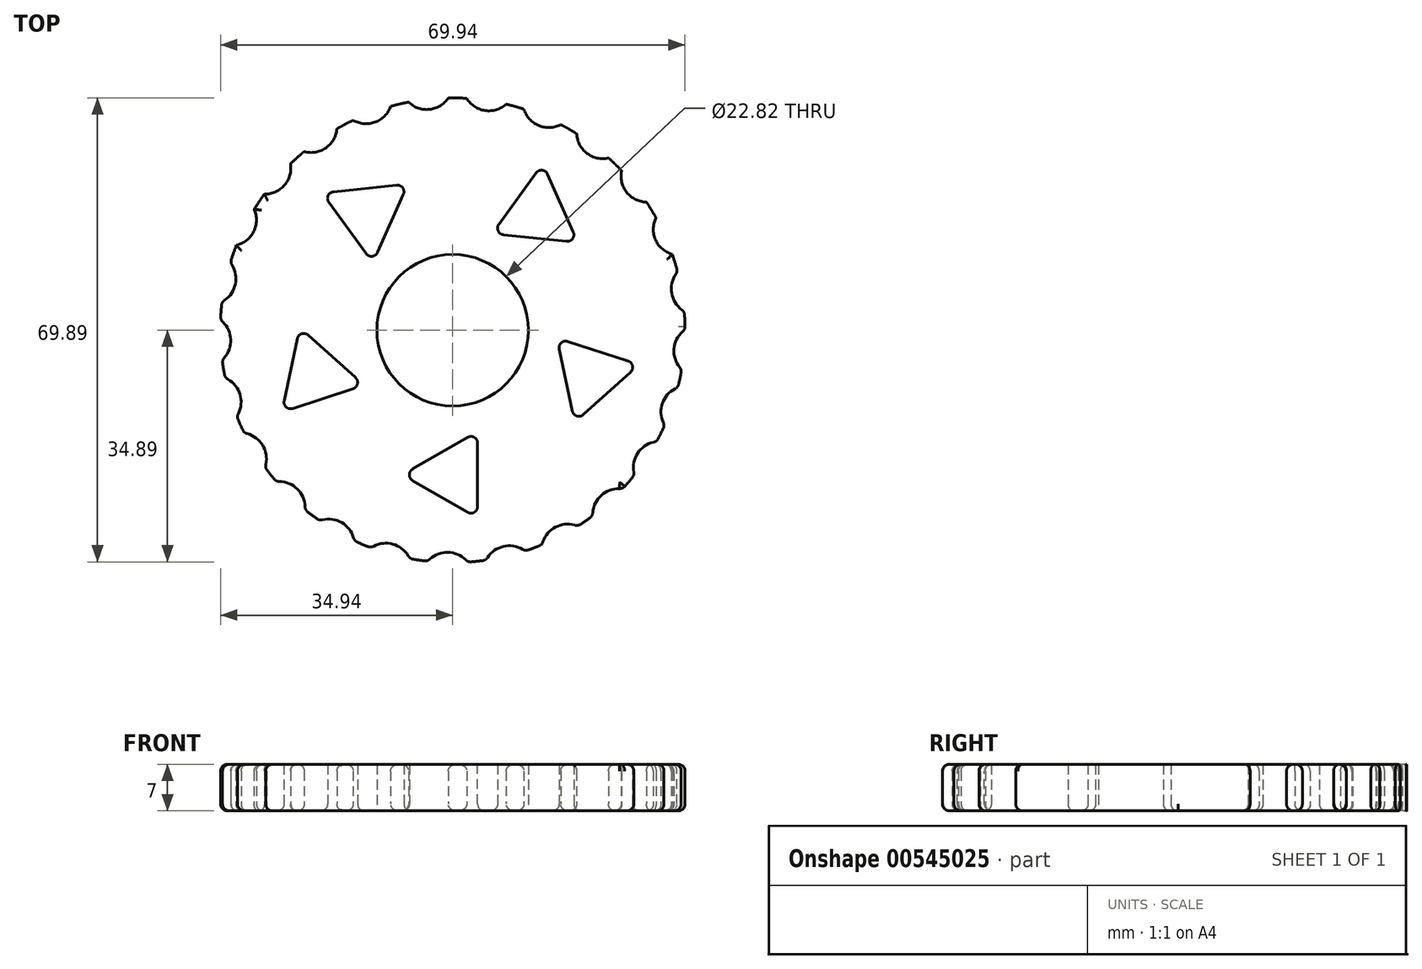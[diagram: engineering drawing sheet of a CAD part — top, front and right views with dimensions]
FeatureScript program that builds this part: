
annotation { "Feature Type Name" : "Feature", "Feature Type Description" : "" }
export const myFeature = defineFeature(function(context is Context, id is Id, definition is map)
    precondition{}
    {
        {
            var Q0;
            Q0=qCreatedBy(makeId("Top.planeOp"),FACE);
            var sketch = newSketch(context, id + "F0", { "sketchPlane" : qUnion([Q0])});
            skCircle(sketch, "E0", {"center": v(0, 0) * mm, "radius": 35 * mm});
            skCircle(sketch, "E1", {"center": v(0, 0) * mm, "radius": 11.41 * mm});
            skCircle(sketch, "E2", {"center": v(-36.54, 7.77) * mm, "radius": 3.9 * mm});
            skSolve(sketch);
        }
        {
            var Q0;
            Q0=makeQuery(id+"F0.imprint","IMPRINT",FACE,{"disambiguationData":[TD([[makeQuery(id+"F0.imprint","IMPRINT",EDGE,{"derivedFrom":sQuery(id+"F0.wireOp",EDGE,"E1")}),-1.0]])]});
            extrude(context, id + "F1", {"entities" : qUnion([Q0]), "depth" : 7 * mm, "offsetDistance" : 25 * mm});
        }
        {
            var Q0;
            Q0=makeQuery(id+"F1.opExtrude","SWEPT_FACE",FACE,{"disambiguationData":[OSD([sQuery(id+"F0.wireOp",EDGE,"E2")])]});
            var Q1;
            Q1=makeQuery(id+"F1.opExtrude","SWEPT_FACE",FACE,{"disambiguationData":[OSD([sQuery(id+"F0.wireOp",EDGE,"E0")])]});
            circularPattern(context, id + "F2", {"patternType" : PatternType.FACE, "faces" : qUnion([Q0]), "axis" : qUnion([Q1]), "angle" : 360 * degree, "instanceCount" : 25, "oppositeDirection" : true, "equalSpace" : true});
        }
        {
            var Q0;
            Q0=makeQuery(id+"F1.opExtrude","CAP_FACE",FACE,{"disambiguationData":[OSD([sQuery(id+"F0.wireOp",EDGE,"E0"),sQuery(id+"F0.wireOp",EDGE,"E1"),sQuery(id+"F0.wireOp",EDGE,"E2")])],"isStart":false});
            var sketch = newSketch(context, id + "F3", { "sketchPlane" : qUnion([Q0])});
            skCircle(sketch, "E3.cCircle", {"center": v(0, -21.78) * mm, "radius": 3.76 * mm, "construction": true});
            skLineSegment(sketch, "E3.0", {"start": v(3.76, -15.27) * mm, "end": v(3.76, -28.3) * mm});
            skLineSegment(sketch, "E3.1", {"start": v(3.76, -28.3) * mm, "end": v(-7.52, -21.78) * mm});
            skLineSegment(sketch, "E3.2", {"start": v(-7.52, -21.78) * mm, "end": v(3.76, -15.27) * mm});
            skPoint(sketch, "E3.0.midPoint", {"position": v(3.76, -21.78) * mm});
            skSolve(sketch);
        }
        {
            var Q0;
            Q0 = qSketchRegion(id + "F3", true);
            extrude(context, id + "F4", {"entities" : qUnion([Q0]), "operationType" : NewBodyOperationType.REMOVE, "oppositeDirection" : true, "depth" : 25 * mm, "offsetDistance" : 25 * mm});
        }
        {
            var Q0;
            Q0=makeQuery(id+"F4.boolean.opBoolean","COPY",FACE,{"derivedFrom":makeQuery(id+"F4.opExtrude","SWEPT_FACE",FACE,{"disambiguationData":[OSD([sQuery(id+"F3.wireOp",EDGE,"E3.2")])]})});
            var Q1;
            Q1=makeQuery(id+"F4.boolean.opBoolean","COPY",FACE,{"derivedFrom":makeQuery(id+"F4.opExtrude","SWEPT_FACE",FACE,{"disambiguationData":[OSD([sQuery(id+"F3.wireOp",EDGE,"E3.0")])]})});
            var Q2;
            Q2=makeQuery(id+"F4.boolean.opBoolean","COPY",FACE,{"derivedFrom":makeQuery(id+"F4.opExtrude","SWEPT_FACE",FACE,{"disambiguationData":[OSD([sQuery(id+"F3.wireOp",EDGE,"E3.1")])]})});
            var Q3;
            Q3=makeQuery(id+"F1.opExtrude","CAP_EDGE",EDGE,{"disambiguationData":[OSD([sQuery(id+"F0.wireOp",EDGE,"E1")])],"isStart":false});
            circularPattern(context, id + "F5", {"patternType" : PatternType.FACE, "faces" : qUnion([Q0, Q1, Q2]), "axis" : qUnion([Q3]), "angle" : 360 * degree, "instanceCount" : 5, "equalSpace" : true});
        }
        {
            var Q0;
            Q0=makeQuery(id+"F5.opPattern","COPY",EDGE,{"derivedFrom":makeQuery(id+"F4.boolean.opBoolean","COPY",EDGE,{"derivedFrom":makeQuery(id+"F4.opExtrude","SWEPT_EDGE",EDGE,{"disambiguationData":[OSD([sQuery(id+"F3.wireOp",EDGE,"E3.1"),sQuery(id+"F3.wireOp",EDGE,"E3.2")])]})}),"instanceName":"4"});
            var Q1;
            Q1=makeQuery(id+"F5.opPattern","COPY",EDGE,{"derivedFrom":makeQuery(id+"F4.boolean.opBoolean","COPY",EDGE,{"derivedFrom":makeQuery(id+"F4.opExtrude","SWEPT_EDGE",EDGE,{"disambiguationData":[OSD([sQuery(id+"F3.wireOp",EDGE,"E3.0"),sQuery(id+"F3.wireOp",EDGE,"E3.2")])]})}),"instanceName":"4"});
            var Q2;
            Q2=makeQuery(id+"F5.opPattern","COPY",EDGE,{"derivedFrom":makeQuery(id+"F4.boolean.opBoolean","COPY",EDGE,{"derivedFrom":makeQuery(id+"F4.opExtrude","SWEPT_EDGE",EDGE,{"disambiguationData":[OSD([sQuery(id+"F3.wireOp",EDGE,"E3.0"),sQuery(id+"F3.wireOp",EDGE,"E3.1")])]})}),"instanceName":"4"});
            var Q3;
            Q3=makeQuery(id+"F5.opPattern","COPY",EDGE,{"derivedFrom":makeQuery(id+"F4.boolean.opBoolean","COPY",EDGE,{"derivedFrom":makeQuery(id+"F4.opExtrude","SWEPT_EDGE",EDGE,{"disambiguationData":[OSD([sQuery(id+"F3.wireOp",EDGE,"E3.1"),sQuery(id+"F3.wireOp",EDGE,"E3.2")])]})}),"instanceName":"3"});
            var Q4;
            Q4=makeQuery(id+"F5.opPattern","COPY",EDGE,{"derivedFrom":makeQuery(id+"F4.boolean.opBoolean","COPY",EDGE,{"derivedFrom":makeQuery(id+"F4.opExtrude","SWEPT_EDGE",EDGE,{"disambiguationData":[OSD([sQuery(id+"F3.wireOp",EDGE,"E3.0"),sQuery(id+"F3.wireOp",EDGE,"E3.2")])]})}),"instanceName":"3"});
            var Q5;
            Q5=makeQuery(id+"F5.opPattern","COPY",EDGE,{"derivedFrom":makeQuery(id+"F4.boolean.opBoolean","COPY",EDGE,{"derivedFrom":makeQuery(id+"F4.opExtrude","SWEPT_EDGE",EDGE,{"disambiguationData":[OSD([sQuery(id+"F3.wireOp",EDGE,"E3.0"),sQuery(id+"F3.wireOp",EDGE,"E3.1")])]})}),"instanceName":"3"});
            var Q6;
            Q6=makeQuery(id+"F5.opPattern","COPY",EDGE,{"derivedFrom":makeQuery(id+"F4.boolean.opBoolean","COPY",EDGE,{"derivedFrom":makeQuery(id+"F4.opExtrude","SWEPT_EDGE",EDGE,{"disambiguationData":[OSD([sQuery(id+"F3.wireOp",EDGE,"E3.0"),sQuery(id+"F3.wireOp",EDGE,"E3.1")])]})}),"instanceName":"2"});
            var Q7;
            Q7=makeQuery(id+"F5.opPattern","COPY",EDGE,{"derivedFrom":makeQuery(id+"F4.boolean.opBoolean","COPY",EDGE,{"derivedFrom":makeQuery(id+"F4.opExtrude","SWEPT_EDGE",EDGE,{"disambiguationData":[OSD([sQuery(id+"F3.wireOp",EDGE,"E3.1"),sQuery(id+"F3.wireOp",EDGE,"E3.2")])]})}),"instanceName":"2"});
            var Q8;
            Q8=makeQuery(id+"F5.opPattern","COPY",EDGE,{"derivedFrom":makeQuery(id+"F4.boolean.opBoolean","COPY",EDGE,{"derivedFrom":makeQuery(id+"F4.opExtrude","SWEPT_EDGE",EDGE,{"disambiguationData":[OSD([sQuery(id+"F3.wireOp",EDGE,"E3.0"),sQuery(id+"F3.wireOp",EDGE,"E3.2")])]})}),"instanceName":"2"});
            var Q9;
            Q9=makeQuery(id+"F5.opPattern","COPY",EDGE,{"derivedFrom":makeQuery(id+"F4.boolean.opBoolean","COPY",EDGE,{"derivedFrom":makeQuery(id+"F4.opExtrude","SWEPT_EDGE",EDGE,{"disambiguationData":[OSD([sQuery(id+"F3.wireOp",EDGE,"E3.0"),sQuery(id+"F3.wireOp",EDGE,"E3.2")])]})}),"instanceName":"1"});
            var Q10;
            Q10=makeQuery(id+"F5.opPattern","COPY",EDGE,{"derivedFrom":makeQuery(id+"F4.boolean.opBoolean","COPY",EDGE,{"derivedFrom":makeQuery(id+"F4.opExtrude","SWEPT_EDGE",EDGE,{"disambiguationData":[OSD([sQuery(id+"F3.wireOp",EDGE,"E3.0"),sQuery(id+"F3.wireOp",EDGE,"E3.1")])]})}),"instanceName":"1"});
            var Q11;
            Q11=makeQuery(id+"F5.opPattern","COPY",EDGE,{"derivedFrom":makeQuery(id+"F4.boolean.opBoolean","COPY",EDGE,{"derivedFrom":makeQuery(id+"F4.opExtrude","SWEPT_EDGE",EDGE,{"disambiguationData":[OSD([sQuery(id+"F3.wireOp",EDGE,"E3.1"),sQuery(id+"F3.wireOp",EDGE,"E3.2")])]})}),"instanceName":"1"});
            var Q12;
            Q12=makeQuery(id+"F4.boolean.opBoolean","COPY",EDGE,{"derivedFrom":makeQuery(id+"F4.opExtrude","SWEPT_EDGE",EDGE,{"disambiguationData":[OSD([sQuery(id+"F3.wireOp",EDGE,"E3.0"),sQuery(id+"F3.wireOp",EDGE,"E3.2")])]})});
            var Q13;
            Q13=makeQuery(id+"F4.boolean.opBoolean","COPY",EDGE,{"derivedFrom":makeQuery(id+"F4.opExtrude","SWEPT_EDGE",EDGE,{"disambiguationData":[OSD([sQuery(id+"F3.wireOp",EDGE,"E3.1"),sQuery(id+"F3.wireOp",EDGE,"E3.2")])]})});
            var Q14;
            Q14=makeQuery(id+"F4.boolean.opBoolean","COPY",EDGE,{"derivedFrom":makeQuery(id+"F4.opExtrude","SWEPT_EDGE",EDGE,{"disambiguationData":[OSD([sQuery(id+"F3.wireOp",EDGE,"E3.0"),sQuery(id+"F3.wireOp",EDGE,"E3.1")])]})});
            var Q15;
            {var subQ0=sQuery(id+"F0.wireOp",EDGE,"E2");var subQ1=sQuery(id+"F0.wireOp",EDGE,"E0");Q15=makeQuery(id+"F2.opPattern","COPY",EDGE,{"derivedFrom":makeQuery(id+"F1.opExtrude","SWEPT_EDGE",EDGE,{"disambiguationData":[OSD([subQ1,subQ0]),TDD([makeQuery(id+"F0.imprint","INTERSECT",VERTEX,{"disambiguationData":[OD(1.0)],"derivedFrom":[subQ1,subQ0]})])]}),"instanceName":"3"});}
            var Q16;
            {var subQ0=sQuery(id+"F0.wireOp",EDGE,"E2");var subQ1=sQuery(id+"F0.wireOp",EDGE,"E0");Q16=makeQuery(id+"F2.opPattern","COPY",EDGE,{"derivedFrom":makeQuery(id+"F1.opExtrude","SWEPT_EDGE",EDGE,{"disambiguationData":[OSD([subQ1,subQ0]),TDD([makeQuery(id+"F0.imprint","INTERSECT",VERTEX,{"disambiguationData":[OD(0.0)],"derivedFrom":[subQ1,subQ0]})])]}),"instanceName":"2"});}
            var Q17;
            {var subQ0=sQuery(id+"F0.wireOp",EDGE,"E2");var subQ1=sQuery(id+"F0.wireOp",EDGE,"E0");Q17=makeQuery(id+"F2.opPattern","COPY",EDGE,{"derivedFrom":makeQuery(id+"F1.opExtrude","SWEPT_EDGE",EDGE,{"disambiguationData":[OSD([subQ1,subQ0]),TDD([makeQuery(id+"F0.imprint","INTERSECT",VERTEX,{"disambiguationData":[OD(0.0)],"derivedFrom":[subQ1,subQ0]})])]}),"instanceName":"3"});}
            var Q18;
            {var subQ0=sQuery(id+"F0.wireOp",EDGE,"E2");var subQ1=sQuery(id+"F0.wireOp",EDGE,"E0");Q18=makeQuery(id+"F2.opPattern","COPY",EDGE,{"derivedFrom":makeQuery(id+"F1.opExtrude","SWEPT_EDGE",EDGE,{"disambiguationData":[OSD([subQ1,subQ0]),TDD([makeQuery(id+"F0.imprint","INTERSECT",VERTEX,{"disambiguationData":[OD(1.0)],"derivedFrom":[subQ1,subQ0]})])]}),"instanceName":"4"});}
            var Q19;
            {var subQ0=sQuery(id+"F0.wireOp",EDGE,"E2");var subQ1=sQuery(id+"F0.wireOp",EDGE,"E0");Q19=makeQuery(id+"F2.opPattern","COPY",EDGE,{"derivedFrom":makeQuery(id+"F1.opExtrude","SWEPT_EDGE",EDGE,{"disambiguationData":[OSD([subQ1,subQ0]),TDD([makeQuery(id+"F0.imprint","INTERSECT",VERTEX,{"disambiguationData":[OD(0.0)],"derivedFrom":[subQ1,subQ0]})])]}),"instanceName":"4"});}
            var Q20;
            {var subQ0=sQuery(id+"F0.wireOp",EDGE,"E2");var subQ1=sQuery(id+"F0.wireOp",EDGE,"E0");Q20=makeQuery(id+"F2.opPattern","COPY",EDGE,{"derivedFrom":makeQuery(id+"F1.opExtrude","SWEPT_EDGE",EDGE,{"disambiguationData":[OSD([subQ1,subQ0]),TDD([makeQuery(id+"F0.imprint","INTERSECT",VERTEX,{"disambiguationData":[OD(1.0)],"derivedFrom":[subQ1,subQ0]})])]}),"instanceName":"5"});}
            var Q21;
            {var subQ0=sQuery(id+"F0.wireOp",EDGE,"E2");var subQ1=sQuery(id+"F0.wireOp",EDGE,"E0");Q21=makeQuery(id+"F2.opPattern","COPY",EDGE,{"derivedFrom":makeQuery(id+"F1.opExtrude","SWEPT_EDGE",EDGE,{"disambiguationData":[OSD([subQ1,subQ0]),TDD([makeQuery(id+"F0.imprint","INTERSECT",VERTEX,{"disambiguationData":[OD(0.0)],"derivedFrom":[subQ1,subQ0]})])]}),"instanceName":"5"});}
            var Q22;
            {var subQ0=sQuery(id+"F0.wireOp",EDGE,"E2");var subQ1=sQuery(id+"F0.wireOp",EDGE,"E0");Q22=makeQuery(id+"F2.opPattern","COPY",EDGE,{"derivedFrom":makeQuery(id+"F1.opExtrude","SWEPT_EDGE",EDGE,{"disambiguationData":[OSD([subQ1,subQ0]),TDD([makeQuery(id+"F0.imprint","INTERSECT",VERTEX,{"disambiguationData":[OD(1.0)],"derivedFrom":[subQ1,subQ0]})])]}),"instanceName":"6"});}
            var Q23;
            {var subQ0=sQuery(id+"F0.wireOp",EDGE,"E2");var subQ1=sQuery(id+"F0.wireOp",EDGE,"E0");Q23=makeQuery(id+"F2.opPattern","COPY",EDGE,{"derivedFrom":makeQuery(id+"F1.opExtrude","SWEPT_EDGE",EDGE,{"disambiguationData":[OSD([subQ1,subQ0]),TDD([makeQuery(id+"F0.imprint","INTERSECT",VERTEX,{"disambiguationData":[OD(0.0)],"derivedFrom":[subQ1,subQ0]})])]}),"instanceName":"6"});}
            var Q24;
            {var subQ0=sQuery(id+"F0.wireOp",EDGE,"E2");var subQ1=sQuery(id+"F0.wireOp",EDGE,"E0");Q24=makeQuery(id+"F2.opPattern","COPY",EDGE,{"derivedFrom":makeQuery(id+"F1.opExtrude","SWEPT_EDGE",EDGE,{"disambiguationData":[OSD([subQ1,subQ0]),TDD([makeQuery(id+"F0.imprint","INTERSECT",VERTEX,{"disambiguationData":[OD(1.0)],"derivedFrom":[subQ1,subQ0]})])]}),"instanceName":"7"});}
            var Q25;
            {var subQ0=sQuery(id+"F0.wireOp",EDGE,"E2");var subQ1=sQuery(id+"F0.wireOp",EDGE,"E0");Q25=makeQuery(id+"F2.opPattern","COPY",EDGE,{"derivedFrom":makeQuery(id+"F1.opExtrude","SWEPT_EDGE",EDGE,{"disambiguationData":[OSD([subQ1,subQ0]),TDD([makeQuery(id+"F0.imprint","INTERSECT",VERTEX,{"disambiguationData":[OD(0.0)],"derivedFrom":[subQ1,subQ0]})])]}),"instanceName":"7"});}
            var Q26;
            {var subQ0=sQuery(id+"F0.wireOp",EDGE,"E2");var subQ1=sQuery(id+"F0.wireOp",EDGE,"E0");Q26=makeQuery(id+"F2.opPattern","COPY",EDGE,{"derivedFrom":makeQuery(id+"F1.opExtrude","SWEPT_EDGE",EDGE,{"disambiguationData":[OSD([subQ1,subQ0]),TDD([makeQuery(id+"F0.imprint","INTERSECT",VERTEX,{"disambiguationData":[OD(1.0)],"derivedFrom":[subQ1,subQ0]})])]}),"instanceName":"8"});}
            var Q27;
            {var subQ0=sQuery(id+"F0.wireOp",EDGE,"E2");var subQ1=sQuery(id+"F0.wireOp",EDGE,"E0");Q27=makeQuery(id+"F2.opPattern","COPY",EDGE,{"derivedFrom":makeQuery(id+"F1.opExtrude","SWEPT_EDGE",EDGE,{"disambiguationData":[OSD([subQ1,subQ0]),TDD([makeQuery(id+"F0.imprint","INTERSECT",VERTEX,{"disambiguationData":[OD(0.0)],"derivedFrom":[subQ1,subQ0]})])]}),"instanceName":"8"});}
            var Q28;
            {var subQ0=sQuery(id+"F0.wireOp",EDGE,"E2");var subQ1=sQuery(id+"F0.wireOp",EDGE,"E0");Q28=makeQuery(id+"F2.opPattern","COPY",EDGE,{"derivedFrom":makeQuery(id+"F1.opExtrude","SWEPT_EDGE",EDGE,{"disambiguationData":[OSD([subQ1,subQ0]),TDD([makeQuery(id+"F0.imprint","INTERSECT",VERTEX,{"disambiguationData":[OD(1.0)],"derivedFrom":[subQ1,subQ0]})])]}),"instanceName":"9"});}
            var Q29;
            {var subQ0=sQuery(id+"F0.wireOp",EDGE,"E2");var subQ1=sQuery(id+"F0.wireOp",EDGE,"E0");Q29=makeQuery(id+"F2.opPattern","COPY",EDGE,{"derivedFrom":makeQuery(id+"F1.opExtrude","SWEPT_EDGE",EDGE,{"disambiguationData":[OSD([subQ1,subQ0]),TDD([makeQuery(id+"F0.imprint","INTERSECT",VERTEX,{"disambiguationData":[OD(0.0)],"derivedFrom":[subQ1,subQ0]})])]}),"instanceName":"9"});}
            var Q30;
            {var subQ0=sQuery(id+"F0.wireOp",EDGE,"E2");var subQ1=sQuery(id+"F0.wireOp",EDGE,"E0");Q30=makeQuery(id+"F2.opPattern","COPY",EDGE,{"derivedFrom":makeQuery(id+"F1.opExtrude","SWEPT_EDGE",EDGE,{"disambiguationData":[OSD([subQ1,subQ0]),TDD([makeQuery(id+"F0.imprint","INTERSECT",VERTEX,{"disambiguationData":[OD(1.0)],"derivedFrom":[subQ1,subQ0]})])]}),"instanceName":"10"});}
            var Q31;
            {var subQ0=sQuery(id+"F0.wireOp",EDGE,"E2");var subQ1=sQuery(id+"F0.wireOp",EDGE,"E0");Q31=makeQuery(id+"F2.opPattern","COPY",EDGE,{"derivedFrom":makeQuery(id+"F1.opExtrude","SWEPT_EDGE",EDGE,{"disambiguationData":[OSD([subQ1,subQ0]),TDD([makeQuery(id+"F0.imprint","INTERSECT",VERTEX,{"disambiguationData":[OD(0.0)],"derivedFrom":[subQ1,subQ0]})])]}),"instanceName":"10"});}
            var Q32;
            {var subQ0=sQuery(id+"F0.wireOp",EDGE,"E2");var subQ1=sQuery(id+"F0.wireOp",EDGE,"E0");Q32=makeQuery(id+"F2.opPattern","COPY",EDGE,{"derivedFrom":makeQuery(id+"F1.opExtrude","SWEPT_EDGE",EDGE,{"disambiguationData":[OSD([subQ1,subQ0]),TDD([makeQuery(id+"F0.imprint","INTERSECT",VERTEX,{"disambiguationData":[OD(1.0)],"derivedFrom":[subQ1,subQ0]})])]}),"instanceName":"11"});}
            var Q33;
            {var subQ0=sQuery(id+"F0.wireOp",EDGE,"E2");var subQ1=sQuery(id+"F0.wireOp",EDGE,"E0");Q33=makeQuery(id+"F2.opPattern","COPY",EDGE,{"derivedFrom":makeQuery(id+"F1.opExtrude","SWEPT_EDGE",EDGE,{"disambiguationData":[OSD([subQ1,subQ0]),TDD([makeQuery(id+"F0.imprint","INTERSECT",VERTEX,{"disambiguationData":[OD(0.0)],"derivedFrom":[subQ1,subQ0]})])]}),"instanceName":"11"});}
            var Q34;
            {var subQ0=sQuery(id+"F0.wireOp",EDGE,"E2");var subQ1=sQuery(id+"F0.wireOp",EDGE,"E0");Q34=makeQuery(id+"F2.opPattern","COPY",EDGE,{"derivedFrom":makeQuery(id+"F1.opExtrude","SWEPT_EDGE",EDGE,{"disambiguationData":[OSD([subQ1,subQ0]),TDD([makeQuery(id+"F0.imprint","INTERSECT",VERTEX,{"disambiguationData":[OD(1.0)],"derivedFrom":[subQ1,subQ0]})])]}),"instanceName":"12"});}
            var Q35;
            {var subQ0=sQuery(id+"F0.wireOp",EDGE,"E2");var subQ1=sQuery(id+"F0.wireOp",EDGE,"E0");Q35=makeQuery(id+"F2.opPattern","COPY",EDGE,{"derivedFrom":makeQuery(id+"F1.opExtrude","SWEPT_EDGE",EDGE,{"disambiguationData":[OSD([subQ1,subQ0]),TDD([makeQuery(id+"F0.imprint","INTERSECT",VERTEX,{"disambiguationData":[OD(0.0)],"derivedFrom":[subQ1,subQ0]})])]}),"instanceName":"12"});}
            var Q36;
            {var subQ0=sQuery(id+"F0.wireOp",EDGE,"E2");var subQ1=sQuery(id+"F0.wireOp",EDGE,"E0");Q36=makeQuery(id+"F2.opPattern","COPY",EDGE,{"derivedFrom":makeQuery(id+"F1.opExtrude","SWEPT_EDGE",EDGE,{"disambiguationData":[OSD([subQ1,subQ0]),TDD([makeQuery(id+"F0.imprint","INTERSECT",VERTEX,{"disambiguationData":[OD(1.0)],"derivedFrom":[subQ1,subQ0]})])]}),"instanceName":"13"});}
            var Q37;
            {var subQ0=sQuery(id+"F0.wireOp",EDGE,"E2");var subQ1=sQuery(id+"F0.wireOp",EDGE,"E0");Q37=makeQuery(id+"F2.opPattern","COPY",EDGE,{"derivedFrom":makeQuery(id+"F1.opExtrude","SWEPT_EDGE",EDGE,{"disambiguationData":[OSD([subQ1,subQ0]),TDD([makeQuery(id+"F0.imprint","INTERSECT",VERTEX,{"disambiguationData":[OD(0.0)],"derivedFrom":[subQ1,subQ0]})])]}),"instanceName":"13"});}
            var Q38;
            {var subQ0=sQuery(id+"F0.wireOp",EDGE,"E2");var subQ1=sQuery(id+"F0.wireOp",EDGE,"E0");Q38=makeQuery(id+"F2.opPattern","COPY",EDGE,{"derivedFrom":makeQuery(id+"F1.opExtrude","SWEPT_EDGE",EDGE,{"disambiguationData":[OSD([subQ1,subQ0]),TDD([makeQuery(id+"F0.imprint","INTERSECT",VERTEX,{"disambiguationData":[OD(1.0)],"derivedFrom":[subQ1,subQ0]})])]}),"instanceName":"14"});}
            var Q39;
            {var subQ0=sQuery(id+"F0.wireOp",EDGE,"E2");var subQ1=sQuery(id+"F0.wireOp",EDGE,"E0");Q39=makeQuery(id+"F2.opPattern","COPY",EDGE,{"derivedFrom":makeQuery(id+"F1.opExtrude","SWEPT_EDGE",EDGE,{"disambiguationData":[OSD([subQ1,subQ0]),TDD([makeQuery(id+"F0.imprint","INTERSECT",VERTEX,{"disambiguationData":[OD(0.0)],"derivedFrom":[subQ1,subQ0]})])]}),"instanceName":"14"});}
            var Q40;
            {var subQ0=sQuery(id+"F0.wireOp",EDGE,"E2");var subQ1=sQuery(id+"F0.wireOp",EDGE,"E0");Q40=makeQuery(id+"F1.opExtrude","SWEPT_EDGE",EDGE,{"disambiguationData":[OSD([subQ1,subQ0]),TDD([makeQuery(id+"F0.imprint","INTERSECT",VERTEX,{"disambiguationData":[OD(1.0)],"derivedFrom":[subQ1,subQ0]})])]});}
            var Q41;
            {var subQ0=sQuery(id+"F0.wireOp",EDGE,"E2");var subQ1=sQuery(id+"F0.wireOp",EDGE,"E0");Q41=makeQuery(id+"F1.opExtrude","SWEPT_EDGE",EDGE,{"disambiguationData":[OSD([subQ1,subQ0]),TDD([makeQuery(id+"F0.imprint","INTERSECT",VERTEX,{"disambiguationData":[OD(0.0)],"derivedFrom":[subQ1,subQ0]})])]});}
            var Q42;
            {var subQ0=sQuery(id+"F0.wireOp",EDGE,"E2");var subQ1=sQuery(id+"F0.wireOp",EDGE,"E0");Q42=makeQuery(id+"F2.opPattern","COPY",EDGE,{"derivedFrom":makeQuery(id+"F1.opExtrude","SWEPT_EDGE",EDGE,{"disambiguationData":[OSD([subQ1,subQ0]),TDD([makeQuery(id+"F0.imprint","INTERSECT",VERTEX,{"disambiguationData":[OD(1.0)],"derivedFrom":[subQ1,subQ0]})])]}),"instanceName":"1"});}
            var Q43;
            {var subQ0=sQuery(id+"F0.wireOp",EDGE,"E2");var subQ1=sQuery(id+"F0.wireOp",EDGE,"E0");Q43=makeQuery(id+"F2.opPattern","COPY",EDGE,{"derivedFrom":makeQuery(id+"F1.opExtrude","SWEPT_EDGE",EDGE,{"disambiguationData":[OSD([subQ1,subQ0]),TDD([makeQuery(id+"F0.imprint","INTERSECT",VERTEX,{"disambiguationData":[OD(0.0)],"derivedFrom":[subQ1,subQ0]})])]}),"instanceName":"1"});}
            var Q44;
            {var subQ0=sQuery(id+"F0.wireOp",EDGE,"E2");var subQ1=sQuery(id+"F0.wireOp",EDGE,"E0");Q44=makeQuery(id+"F2.opPattern","COPY",EDGE,{"derivedFrom":makeQuery(id+"F1.opExtrude","SWEPT_EDGE",EDGE,{"disambiguationData":[OSD([subQ1,subQ0]),TDD([makeQuery(id+"F0.imprint","INTERSECT",VERTEX,{"disambiguationData":[OD(1.0)],"derivedFrom":[subQ1,subQ0]})])]}),"instanceName":"2"});}
            fillet(context, id + "F6", {"entities" : qUnion([Q0, Q1, Q2, Q3, Q4, Q5, Q6, Q7, Q8, Q9, Q10, Q11, Q12, Q13, Q14, Q15, Q16, Q17, Q18, Q19, Q20, Q21, Q22, Q23, Q24, Q25, Q26, Q27, Q28, Q29, Q30, Q31, Q32, Q33, Q34, Q35, Q36, Q37, Q38, Q39, Q40, Q41, Q42, Q43, Q44]), "radius" : 1 * mm, "tangentPropagation" : true, "allowEdgeOverflow" : false});
        }
        {
            var Q0;
            Q0=makeQuery(id+"F4.boolean.opBoolean","COPY",EDGE,{"derivedFrom":makeQuery(id+"F4.opExtrude","CAP_EDGE",EDGE,{"disambiguationData":[OSD([sQuery(id+"F3.wireOp",EDGE,"E3.2")])],"isStart":true})});
            var Q1;
            Q1=makeQuery(id+"F5.opPattern","COPY",EDGE,{"derivedFrom":makeQuery(id+"F4.boolean.opBoolean","COPY",EDGE,{"derivedFrom":makeQuery(id+"F4.opExtrude","CAP_EDGE",EDGE,{"disambiguationData":[OSD([sQuery(id+"F3.wireOp",EDGE,"E3.0")])],"isStart":true})}),"instanceName":"1"});
            var Q2;
            Q2=makeQuery(id+"F5.opPattern","COPY",EDGE,{"derivedFrom":makeQuery(id+"F4.boolean.opBoolean","COPY",EDGE,{"derivedFrom":makeQuery(id+"F4.opExtrude","CAP_EDGE",EDGE,{"disambiguationData":[OSD([sQuery(id+"F3.wireOp",EDGE,"E3.0")])],"isStart":true})}),"instanceName":"2"});
            var Q3;
            Q3=makeQuery(id+"F5.opPattern","COPY",EDGE,{"derivedFrom":makeQuery(id+"F4.boolean.opBoolean","COPY",EDGE,{"derivedFrom":makeQuery(id+"F4.opExtrude","CAP_EDGE",EDGE,{"disambiguationData":[OSD([sQuery(id+"F3.wireOp",EDGE,"E3.1")])],"isStart":true})}),"instanceName":"3"});
            var Q4;
            Q4=makeQuery(id+"F5.opPattern","COPY",EDGE,{"derivedFrom":makeQuery(id+"F4.boolean.opBoolean","COPY",EDGE,{"derivedFrom":makeQuery(id+"F4.opExtrude","CAP_EDGE",EDGE,{"disambiguationData":[OSD([sQuery(id+"F3.wireOp",EDGE,"E3.2")])],"isStart":true})}),"instanceName":"4"});
            var Q5;
            Q5=makeQuery(id+"F2.opPattern","COPY",EDGE,{"derivedFrom":makeQuery(id+"F1.opExtrude","CAP_EDGE",EDGE,{"disambiguationData":[OSD([sQuery(id+"F0.wireOp",EDGE,"E2")])],"isStart":false}),"instanceName":"6"});
            var Q6;
            Q6=makeQuery(id+"F5.opPattern","COPY",EDGE,{"derivedFrom":makeQuery(id+"F4.boolean.opBoolean","INTERSECT",EDGE,{"derivedFrom":[makeQuery(id+"F1.opExtrude","CAP_FACE",FACE,{"disambiguationData":[OSD([sQuery(id+"F0.wireOp",EDGE,"E0"),sQuery(id+"F0.wireOp",EDGE,"E1"),sQuery(id+"F0.wireOp",EDGE,"E2")])],"isStart":true}),makeQuery(id+"F4.opExtrude","SWEPT_FACE",FACE,{"disambiguationData":[OSD([sQuery(id+"F3.wireOp",EDGE,"E3.2")])]})]}),"instanceName":"3"});
            var Q7;
            Q7=makeQuery(id+"F5.opPattern","COPY",EDGE,{"derivedFrom":makeQuery(id+"F4.boolean.opBoolean","INTERSECT",EDGE,{"derivedFrom":[makeQuery(id+"F1.opExtrude","CAP_FACE",FACE,{"disambiguationData":[OSD([sQuery(id+"F0.wireOp",EDGE,"E0"),sQuery(id+"F0.wireOp",EDGE,"E1"),sQuery(id+"F0.wireOp",EDGE,"E2")])],"isStart":true}),makeQuery(id+"F4.opExtrude","SWEPT_FACE",FACE,{"disambiguationData":[OSD([sQuery(id+"F3.wireOp",EDGE,"E3.0")])]})]}),"instanceName":"4"});
            var Q8;
            Q8=makeQuery(id+"F4.boolean.opBoolean","INTERSECT",EDGE,{"derivedFrom":[makeQuery(id+"F1.opExtrude","CAP_FACE",FACE,{"disambiguationData":[OSD([sQuery(id+"F0.wireOp",EDGE,"E0"),sQuery(id+"F0.wireOp",EDGE,"E1"),sQuery(id+"F0.wireOp",EDGE,"E2")])],"isStart":true}),makeQuery(id+"F4.opExtrude","SWEPT_FACE",FACE,{"disambiguationData":[OSD([sQuery(id+"F3.wireOp",EDGE,"E3.0")])]})]});
            var Q9;
            Q9=makeQuery(id+"F5.opPattern","COPY",EDGE,{"derivedFrom":makeQuery(id+"F4.boolean.opBoolean","INTERSECT",EDGE,{"derivedFrom":[makeQuery(id+"F1.opExtrude","CAP_FACE",FACE,{"disambiguationData":[OSD([sQuery(id+"F0.wireOp",EDGE,"E0"),sQuery(id+"F0.wireOp",EDGE,"E1"),sQuery(id+"F0.wireOp",EDGE,"E2")])],"isStart":true}),makeQuery(id+"F4.opExtrude","SWEPT_FACE",FACE,{"disambiguationData":[OSD([sQuery(id+"F3.wireOp",EDGE,"E3.1")])]})]}),"instanceName":"1"});
            var Q10;
            Q10=makeQuery(id+"F5.opPattern","COPY",EDGE,{"derivedFrom":makeQuery(id+"F4.boolean.opBoolean","INTERSECT",EDGE,{"derivedFrom":[makeQuery(id+"F1.opExtrude","CAP_FACE",FACE,{"disambiguationData":[OSD([sQuery(id+"F0.wireOp",EDGE,"E0"),sQuery(id+"F0.wireOp",EDGE,"E1"),sQuery(id+"F0.wireOp",EDGE,"E2")])],"isStart":true}),makeQuery(id+"F4.opExtrude","SWEPT_FACE",FACE,{"disambiguationData":[OSD([sQuery(id+"F3.wireOp",EDGE,"E3.1")])]})]}),"instanceName":"2"});
            var Q11;
            Q11=makeQuery(id+"F2.opPattern","COPY",EDGE,{"derivedFrom":makeQuery(id+"F1.opExtrude","CAP_EDGE",EDGE,{"disambiguationData":[OSD([sQuery(id+"F0.wireOp",EDGE,"E2")])],"isStart":true}),"instanceName":"18"});
            var Q12;
            Q12=makeQuery(id+"F2.opPattern","COPY",EDGE,{"derivedFrom":makeQuery(id+"F1.opExtrude","CAP_EDGE",EDGE,{"disambiguationData":[OSD([sQuery(id+"F0.wireOp",EDGE,"E2")])],"isStart":false}),"instanceName":"21"});
            var Q13;
            Q13=makeQuery(id+"F2.opPattern","COPY",EDGE,{"derivedFrom":makeQuery(id+"F1.opExtrude","CAP_EDGE",EDGE,{"disambiguationData":[OSD([sQuery(id+"F0.wireOp",EDGE,"E2")])],"isStart":false}),"instanceName":"22"});
            var Q14;
            Q14=makeQuery(id+"F2.opPattern","SPLIT",EDGE,{"disambiguationData":[OD(24.0)],"derivedFrom":makeQuery(id+"F1.opExtrude","CAP_EDGE",EDGE,{"disambiguationData":[OSD([sQuery(id+"F0.wireOp",EDGE,"E0")])],"isStart":false})});
            var Q15;
            Q15=makeQuery(id+"F2.opPattern","COPY",EDGE,{"derivedFrom":makeQuery(id+"F1.opExtrude","CAP_EDGE",EDGE,{"disambiguationData":[OSD([sQuery(id+"F0.wireOp",EDGE,"E2")])],"isStart":false}),"instanceName":"23"});
            var Q16;
            Q16=makeQuery(id+"F2.opPattern","COPY",EDGE,{"derivedFrom":makeQuery(id+"F1.opExtrude","CAP_EDGE",EDGE,{"disambiguationData":[OSD([sQuery(id+"F0.wireOp",EDGE,"E2")])],"isStart":false}),"instanceName":"24"});
            var Q17;
            Q17=makeQuery(id+"F2.opPattern","COPY",EDGE,{"derivedFrom":makeQuery(id+"F1.opExtrude","CAP_EDGE",EDGE,{"disambiguationData":[OSD([sQuery(id+"F0.wireOp",EDGE,"E2")])],"isStart":false}),"instanceName":"20"});
            var Q18;
            Q18=makeQuery(id+"F2.opPattern","COPY",EDGE,{"derivedFrom":makeQuery(id+"F1.opExtrude","CAP_EDGE",EDGE,{"disambiguationData":[OSD([sQuery(id+"F0.wireOp",EDGE,"E2")])],"isStart":false}),"instanceName":"19"});
            var Q19;
            Q19=makeQuery(id+"F2.opPattern","COPY",EDGE,{"derivedFrom":makeQuery(id+"F1.opExtrude","CAP_EDGE",EDGE,{"disambiguationData":[OSD([sQuery(id+"F0.wireOp",EDGE,"E2")])],"isStart":false}),"instanceName":"18"});
            var Q20;
            Q20=makeQuery(id+"F2.opPattern","COPY",EDGE,{"derivedFrom":makeQuery(id+"F1.opExtrude","CAP_EDGE",EDGE,{"disambiguationData":[OSD([sQuery(id+"F0.wireOp",EDGE,"E2")])],"isStart":false}),"instanceName":"17"});
            var Q21;
            Q21=makeQuery(id+"F2.opPattern","COPY",EDGE,{"derivedFrom":makeQuery(id+"F1.opExtrude","CAP_EDGE",EDGE,{"disambiguationData":[OSD([sQuery(id+"F0.wireOp",EDGE,"E2")])],"isStart":false}),"instanceName":"15"});
            var Q22;
            Q22=makeQuery(id+"F2.opPattern","COPY",EDGE,{"derivedFrom":makeQuery(id+"F1.opExtrude","CAP_EDGE",EDGE,{"disambiguationData":[OSD([sQuery(id+"F0.wireOp",EDGE,"E2")])],"isStart":false}),"instanceName":"16"});
            var Q23;
            Q23=makeQuery(id+"F2.opPattern","COPY",EDGE,{"derivedFrom":makeQuery(id+"F1.opExtrude","CAP_EDGE",EDGE,{"disambiguationData":[OSD([sQuery(id+"F0.wireOp",EDGE,"E2")])],"isStart":true}),"instanceName":"17"});
            var Q24;
            Q24=makeQuery(id+"F2.opPattern","COPY",EDGE,{"derivedFrom":makeQuery(id+"F1.opExtrude","CAP_EDGE",EDGE,{"disambiguationData":[OSD([sQuery(id+"F0.wireOp",EDGE,"E2")])],"isStart":true}),"instanceName":"16"});
            var Q25;
            Q25=makeQuery(id+"F2.opPattern","COPY",EDGE,{"derivedFrom":makeQuery(id+"F1.opExtrude","CAP_EDGE",EDGE,{"disambiguationData":[OSD([sQuery(id+"F0.wireOp",EDGE,"E2")])],"isStart":true}),"instanceName":"15"});
            var Q26;
            Q26=makeQuery(id+"F2.opPattern","COPY",EDGE,{"derivedFrom":makeQuery(id+"F1.opExtrude","CAP_EDGE",EDGE,{"disambiguationData":[OSD([sQuery(id+"F0.wireOp",EDGE,"E2")])],"isStart":true}),"instanceName":"14"});
            var Q27;
            Q27=makeQuery(id+"F2.opPattern","COPY",EDGE,{"derivedFrom":makeQuery(id+"F1.opExtrude","CAP_EDGE",EDGE,{"disambiguationData":[OSD([sQuery(id+"F0.wireOp",EDGE,"E2")])],"isStart":true}),"instanceName":"13"});
            var Q28;
            Q28=makeQuery(id+"F2.opPattern","COPY",EDGE,{"derivedFrom":makeQuery(id+"F1.opExtrude","CAP_EDGE",EDGE,{"disambiguationData":[OSD([sQuery(id+"F0.wireOp",EDGE,"E2")])],"isStart":true}),"instanceName":"12"});
            var Q29;
            Q29=makeQuery(id+"F2.opPattern","COPY",EDGE,{"derivedFrom":makeQuery(id+"F1.opExtrude","CAP_EDGE",EDGE,{"disambiguationData":[OSD([sQuery(id+"F0.wireOp",EDGE,"E2")])],"isStart":true}),"instanceName":"11"});
            var Q30;
            Q30=makeQuery(id+"F2.opPattern","COPY",EDGE,{"derivedFrom":makeQuery(id+"F1.opExtrude","CAP_EDGE",EDGE,{"disambiguationData":[OSD([sQuery(id+"F0.wireOp",EDGE,"E2")])],"isStart":true}),"instanceName":"19"});
            var Q31;
            Q31=makeQuery(id+"F2.opPattern","COPY",EDGE,{"derivedFrom":makeQuery(id+"F1.opExtrude","CAP_EDGE",EDGE,{"disambiguationData":[OSD([sQuery(id+"F0.wireOp",EDGE,"E2")])],"isStart":true}),"instanceName":"20"});
            var Q32;
            Q32=makeQuery(id+"F2.opPattern","COPY",EDGE,{"derivedFrom":makeQuery(id+"F1.opExtrude","CAP_EDGE",EDGE,{"disambiguationData":[OSD([sQuery(id+"F0.wireOp",EDGE,"E2")])],"isStart":true}),"instanceName":"21"});
            var Q33;
            Q33=makeQuery(id+"F2.opPattern","COPY",EDGE,{"derivedFrom":makeQuery(id+"F1.opExtrude","CAP_EDGE",EDGE,{"disambiguationData":[OSD([sQuery(id+"F0.wireOp",EDGE,"E2")])],"isStart":true}),"instanceName":"22"});
            var Q34;
            Q34=makeQuery(id+"F2.opPattern","COPY",EDGE,{"derivedFrom":makeQuery(id+"F1.opExtrude","CAP_EDGE",EDGE,{"disambiguationData":[OSD([sQuery(id+"F0.wireOp",EDGE,"E2")])],"isStart":true}),"instanceName":"23"});
            var Q35;
            Q35=makeQuery(id+"F2.opPattern","COPY",EDGE,{"derivedFrom":makeQuery(id+"F1.opExtrude","CAP_EDGE",EDGE,{"disambiguationData":[OSD([sQuery(id+"F0.wireOp",EDGE,"E2")])],"isStart":true}),"instanceName":"24"});
            fillet(context, id + "F7", {"entities" : qUnion([Q0, Q1, Q2, Q3, Q4, Q5, Q6, Q7, Q8, Q9, Q10, Q11, Q12, Q13, Q14, Q15, Q16, Q17, Q18, Q19, Q20, Q21, Q22, Q23, Q24, Q25, Q26, Q27, Q28, Q29, Q30, Q31, Q32, Q33, Q34, Q35]), "radius" : 1 * mm, "tangentPropagation" : true, "allowEdgeOverflow" : false});
        }
    });
